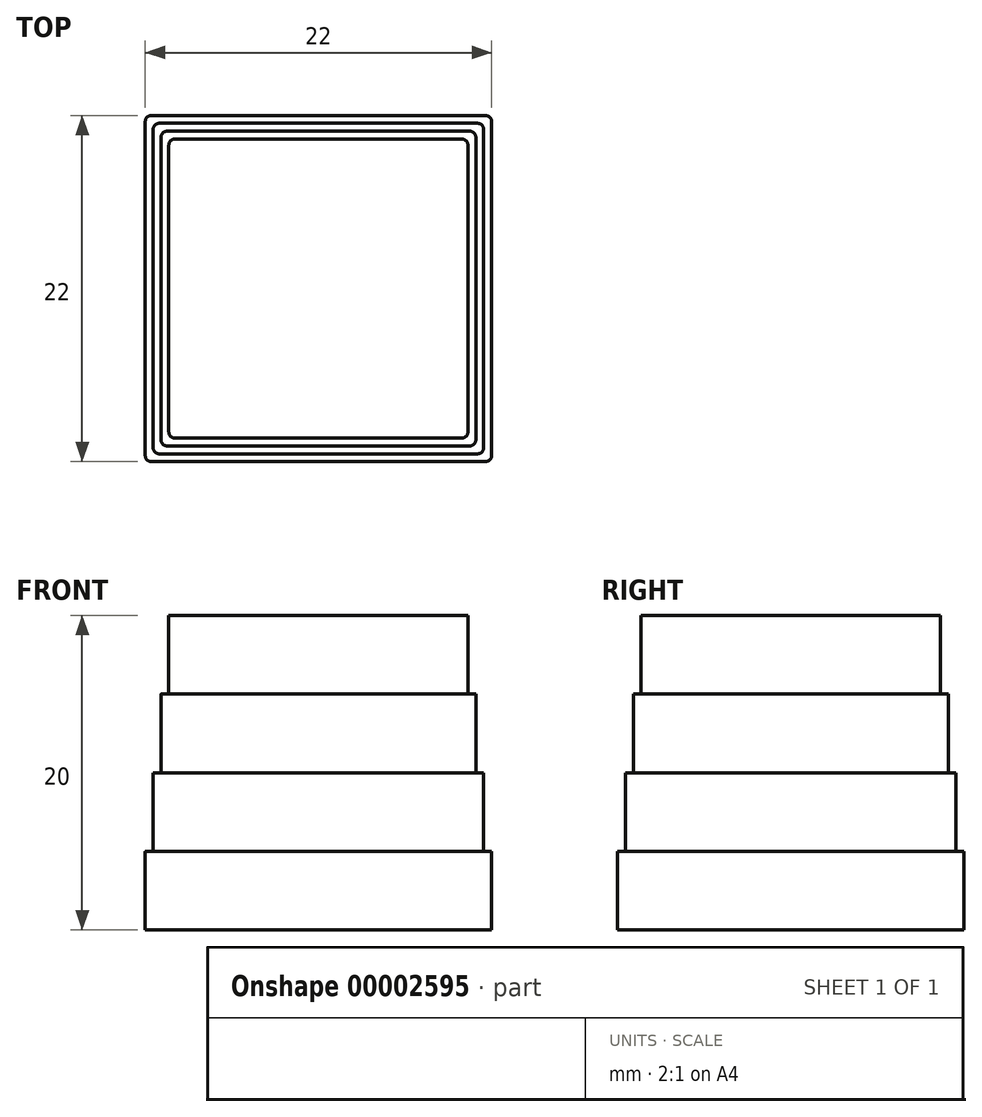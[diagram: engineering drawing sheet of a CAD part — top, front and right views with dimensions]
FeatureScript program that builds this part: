
annotation { "Feature Type Name" : "Feature", "Feature Type Description" : "" }
export const myFeature = defineFeature(function(context is Context, id is Id, definition is map)
    precondition{}
    {
        {
            var Q0;
            Q0=qCreatedBy(makeId("Top.planeOp"),FACE);
            var sketch = newSketch(context, id + "F0", { "sketchPlane" : qUnion([Q0])});
            skLineSegment(sketch, "E0.rect.bottom", {"start": v(9.1, -9.5) * mm, "end": v(-9.1, -9.5) * mm});
            skLineSegment(sketch, "E0.rect.top", {"start": v(9.1, 9.5) * mm, "end": v(-9.1, 9.5) * mm});
            skLineSegment(sketch, "E0.rect.left", {"start": v(9.5, -9.1) * mm, "end": v(9.5, 9.1) * mm});
            skLineSegment(sketch, "E0.rect.right", {"start": v(-9.5, -9.1) * mm, "end": v(-9.5, 9.1) * mm});
            skPoint(sketch, "E0.rect.middle", {"position": v(0, 0) * mm});
            skLineSegment(sketch, "E1.rect.bottom", {"start": v(-9.6, 10) * mm, "end": v(9.6, 10) * mm});
            skLineSegment(sketch, "E1.rect.top", {"start": v(-9.6, -10) * mm, "end": v(9.6, -10) * mm});
            skLineSegment(sketch, "E1.rect.left", {"start": v(-10, 9.6) * mm, "end": v(-10, -9.6) * mm});
            skLineSegment(sketch, "E1.rect.right", {"start": v(10, 9.6) * mm, "end": v(10, -9.6) * mm});
            skLineSegment(sketch, "E2.rect.bottom", {"start": v(-10.1, 10.5) * mm, "end": v(10.1, 10.5) * mm});
            skLineSegment(sketch, "E2.rect.top", {"start": v(-10.1, -10.5) * mm, "end": v(10.1, -10.5) * mm});
            skLineSegment(sketch, "E2.rect.left", {"start": v(-10.5, 10.1) * mm, "end": v(-10.5, -10.1) * mm});
            skLineSegment(sketch, "E2.rect.right", {"start": v(10.5, 10.1) * mm, "end": v(10.5, -10.1) * mm});
            skLineSegment(sketch, "E3.rect.bottom", {"start": v(-10.6, 11) * mm, "end": v(10.6, 11) * mm});
            skLineSegment(sketch, "E3.rect.top", {"start": v(-10.6, -11) * mm, "end": v(10.6, -11) * mm});
            skLineSegment(sketch, "E3.rect.left", {"start": v(-11, 10.6) * mm, "end": v(-11, -10.6) * mm});
            skLineSegment(sketch, "E3.rect.right", {"start": v(11, 10.6) * mm, "end": v(11, -10.6) * mm});
            skPoint(sketch, "E4.visualSharp", {"position": v(-9.5, 9.5) * mm});
            skArc(sketch, "E4.filletArc", {"start": v(-9.1, 9.5) * mm, "mid": v(-9.38, 9.38) * mm, "end": v(-9.5, 9.1) * mm});
            skPoint(sketch, "E5.visualSharp", {"position": v(9.5, 9.5) * mm});
            skArc(sketch, "E5.filletArc", {"start": v(9.5, 9.1) * mm, "mid": v(9.38, 9.38) * mm, "end": v(9.1, 9.5) * mm});
            skPoint(sketch, "E6.visualSharp", {"position": v(9.5, -9.5) * mm});
            skArc(sketch, "E6.filletArc", {"start": v(9.1, -9.5) * mm, "mid": v(9.38, -9.38) * mm, "end": v(9.5, -9.1) * mm});
            skPoint(sketch, "E7.visualSharp", {"position": v(-9.5, -9.5) * mm});
            skArc(sketch, "E7.filletArc", {"start": v(-9.5, -9.1) * mm, "mid": v(-9.38, -9.38) * mm, "end": v(-9.1, -9.5) * mm});
            skPoint(sketch, "E8.visualSharp", {"position": v(-10, -10) * mm});
            skArc(sketch, "E8.filletArc", {"start": v(-10, -9.6) * mm, "mid": v(-9.88, -9.88) * mm, "end": v(-9.6, -10) * mm});
            skPoint(sketch, "E9.visualSharp", {"position": v(-10.5, -10.5) * mm});
            skArc(sketch, "E9.filletArc", {"start": v(-10.5, -10.1) * mm, "mid": v(-10.38, -10.38) * mm, "end": v(-10.1, -10.5) * mm});
            skPoint(sketch, "E10.visualSharp", {"position": v(-11, -11) * mm});
            skArc(sketch, "E10.filletArc", {"start": v(-11, -10.6) * mm, "mid": v(-10.88, -10.88) * mm, "end": v(-10.6, -11) * mm});
            skPoint(sketch, "E11.visualSharp", {"position": v(10, -10) * mm});
            skArc(sketch, "E11.filletArc", {"start": v(9.6, -10) * mm, "mid": v(9.88, -9.88) * mm, "end": v(10, -9.6) * mm});
            skPoint(sketch, "E12.visualSharp", {"position": v(10.5, -10.5) * mm});
            skArc(sketch, "E12.filletArc", {"start": v(10.1, -10.5) * mm, "mid": v(10.38, -10.38) * mm, "end": v(10.5, -10.1) * mm});
            skPoint(sketch, "E13.visualSharp", {"position": v(11, -11) * mm});
            skArc(sketch, "E13.filletArc", {"start": v(10.6, -11) * mm, "mid": v(10.88, -10.88) * mm, "end": v(11, -10.6) * mm});
            skPoint(sketch, "E14.visualSharp", {"position": v(10, 10) * mm});
            skArc(sketch, "E14.filletArc", {"start": v(10, 9.6) * mm, "mid": v(9.88, 9.88) * mm, "end": v(9.6, 10) * mm});
            skPoint(sketch, "E15.visualSharp", {"position": v(10.5, 10.5) * mm});
            skArc(sketch, "E15.filletArc", {"start": v(10.5, 10.1) * mm, "mid": v(10.38, 10.38) * mm, "end": v(10.1, 10.5) * mm});
            skPoint(sketch, "E16.visualSharp", {"position": v(11, 11) * mm});
            skArc(sketch, "E16.filletArc", {"start": v(11, 10.6) * mm, "mid": v(10.88, 10.88) * mm, "end": v(10.6, 11) * mm});
            skPoint(sketch, "E17.visualSharp", {"position": v(-11, 11) * mm});
            skArc(sketch, "E17.filletArc", {"start": v(-10.6, 11) * mm, "mid": v(-10.88, 10.88) * mm, "end": v(-11, 10.6) * mm});
            skPoint(sketch, "E18.visualSharp", {"position": v(-10, 10) * mm});
            skArc(sketch, "E18.filletArc", {"start": v(-9.6, 10) * mm, "mid": v(-9.88, 9.88) * mm, "end": v(-10, 9.6) * mm});
            skPoint(sketch, "E19.visualSharp", {"position": v(-10.5, 10.5) * mm});
            skArc(sketch, "E19.filletArc", {"start": v(-10.1, 10.5) * mm, "mid": v(-10.38, 10.38) * mm, "end": v(-10.5, 10.1) * mm});
            skSolve(sketch);
        }
        {
            var Q0;
            Q0=makeQuery(id+"F0.imprint","IMPRINT",FACE,{"disambiguationData":[TD([[makeQuery(id+"F0.imprint","IMPRINT",EDGE,{"derivedFrom":sQuery(id+"F0.wireOp",EDGE,"E0.rect.bottom")}),-1.0]])]});
            extrude(context, id + "F1", {"entities" : qUnion([Q0]), "depth" : 20 * mm});
        }
        {
            var Q0;
            Q0=makeQuery(id+"F0.imprint","IMPRINT",FACE,{"disambiguationData":[TD([[makeQuery(id+"F0.imprint","IMPRINT",EDGE,{"derivedFrom":sQuery(id+"F0.wireOp",EDGE,"E0.rect.bottom")}),1.0]])]});
            extrude(context, id + "F2", {"entities" : qUnion([Q0]), "operationType" : NewBodyOperationType.ADD, "depth" : 15 * mm});
        }
        {
            var Q0;
            Q0=makeQuery(id+"F0.imprint","IMPRINT",FACE,{"disambiguationData":[TD([[makeQuery(id+"F0.imprint","IMPRINT",EDGE,{"derivedFrom":sQuery(id+"F0.wireOp",EDGE,"E1.rect.bottom")}),1.0]])]});
            extrude(context, id + "F3", {"entities" : qUnion([Q0]), "operationType" : NewBodyOperationType.ADD, "depth" : 10 * mm});
        }
        {
            var Q0;
            Q0=makeQuery(id+"F0.imprint","IMPRINT",FACE,{"disambiguationData":[TD([[makeQuery(id+"F0.imprint","IMPRINT",EDGE,{"derivedFrom":sQuery(id+"F0.wireOp",EDGE,"E2.rect.bottom")}),1.0]])]});
            extrude(context, id + "F4", {"entities" : qUnion([Q0]), "operationType" : NewBodyOperationType.ADD, "depth" : 5 * mm});
        }
    });
